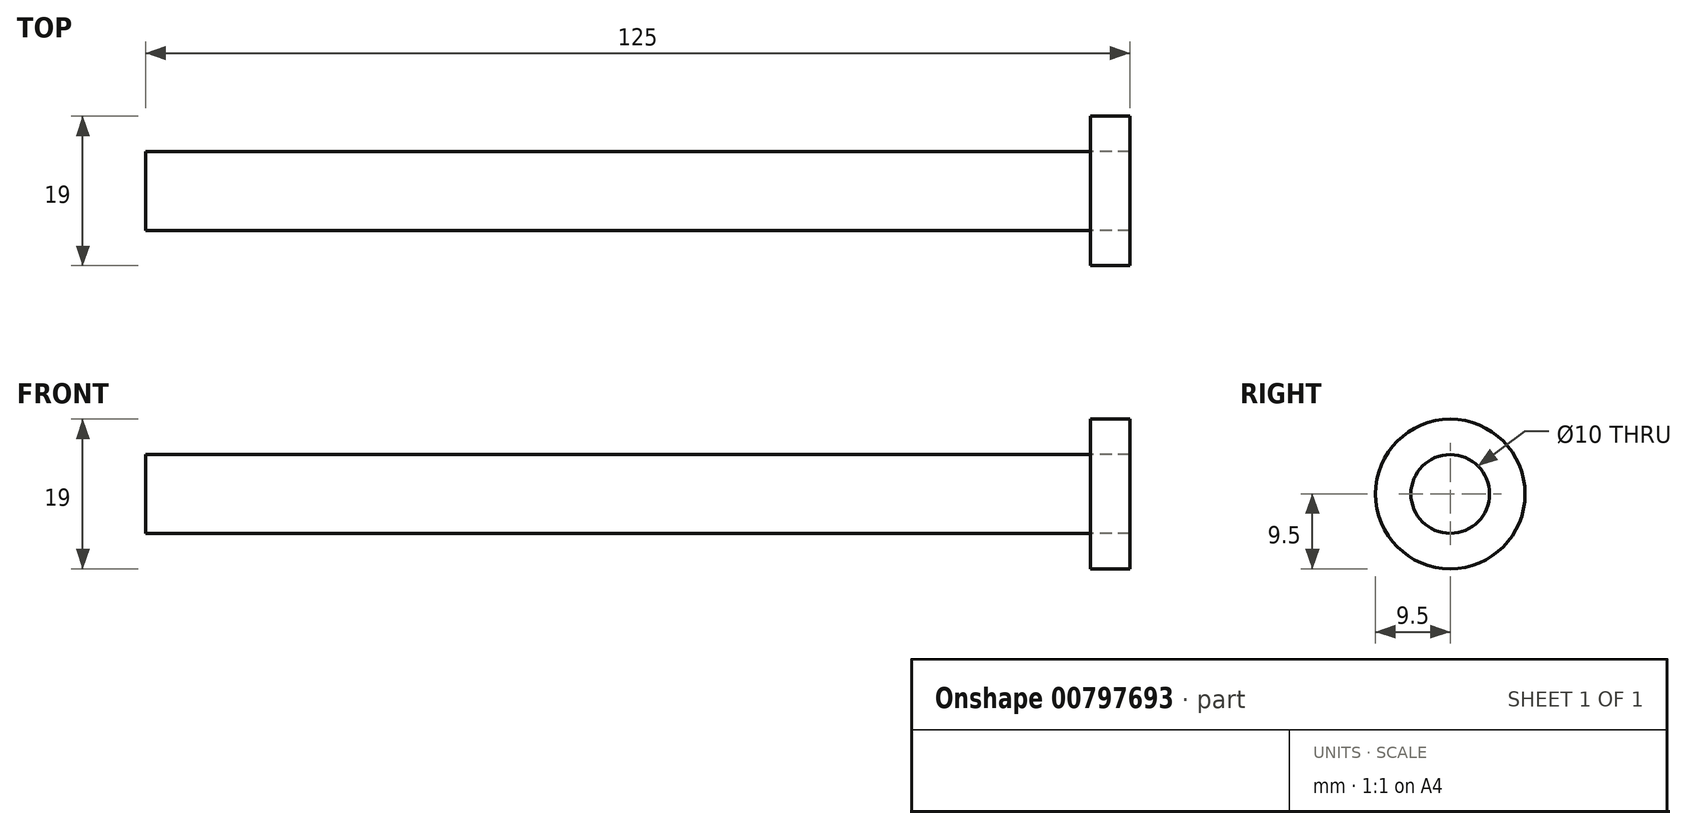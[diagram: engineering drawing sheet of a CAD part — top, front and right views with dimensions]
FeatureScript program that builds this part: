
annotation { "Feature Type Name" : "Feature", "Feature Type Description" : "" }
export const myFeature = defineFeature(function(context is Context, id is Id, definition is map)
    precondition{}
    {
        {
            var Q0;
            Q0=qCreatedBy(makeId("Right.planeOp"),FACE);
            var sketch = newSketch(context, id + "F0", { "sketchPlane" : qUnion([Q0])});
            skCircle(sketch, "E0", {"center": v(0, 0) * mm, "radius": 5 * mm});
            skSolve(sketch);
        }
        {
            var Q0;
            Q0=makeQuery(id+"F0.imprint","IMPRINT",FACE,{"disambiguationData":[TD([[makeQuery(id+"F0.imprint","IMPRINT",EDGE,{"derivedFrom":sQuery(id+"F0.wireOp",EDGE,"E0")}),1.0]])]});
            extrude(context, id + "F1", {"entities" : qUnion([Q0]), "depth" : 120 * mm, "offsetDistance" : 25 * mm});
        }
        {
            var Q0;
            Q0=makeQuery(id+"F1.opExtrude","CAP_FACE",FACE,{"disambiguationData":[OSD([sQuery(id+"F0.wireOp",EDGE,"E0")])],"isStart":false});
            var sketch = newSketch(context, id + "F2", { "sketchPlane" : qUnion([Q0])});
            skCircle(sketch, "E1", {"center": v(0, 0) * mm, "radius": 9.5 * mm});
            skSolve(sketch);
        }
        {
            var Q0;
            Q0=makeQuery(id+"F2.imprint","IMPRINT",FACE,{"disambiguationData":[TD([[makeQuery(id+"F2.imprint","IMPRINT",EDGE,{"derivedFrom":sQuery(id+"F2.wireOp",EDGE,"E1")}),1.0]])]});
            extrude(context, id + "F3", {"entities" : qUnion([Q0]), "depth" : 5 * mm, "offsetDistance" : 25 * mm});
        }
    });
